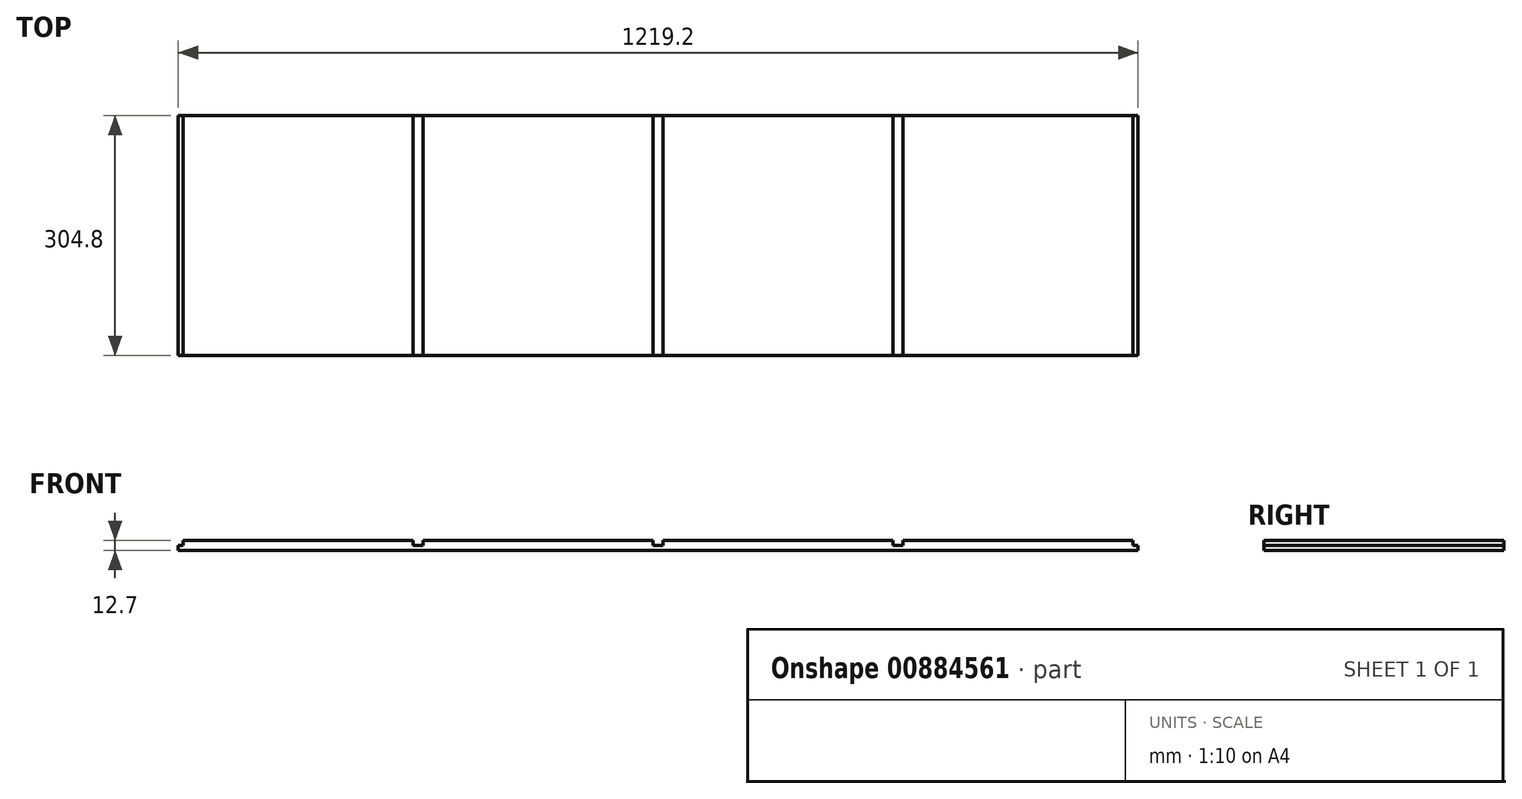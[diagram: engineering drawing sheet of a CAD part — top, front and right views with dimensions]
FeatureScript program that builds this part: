
annotation { "Feature Type Name" : "Feature", "Feature Type Description" : "" }
export const myFeature = defineFeature(function(context is Context, id is Id, definition is map)
    precondition{}
    {
        {
            var Q0;
            Q0=qCreatedBy(makeId("Top.planeOp"),FACE);
            var sketch = newSketch(context, id + "F0", { "sketchPlane" : qUnion([Q0])});
            skLineSegment(sketch, "E0.bottom", {"start": v(-609.6, -152.4) * mm, "end": v(609.6, -152.4) * mm});
            skLineSegment(sketch, "E0.top", {"start": v(-609.6, 152.4) * mm, "end": v(609.6, 152.4) * mm});
            skLineSegment(sketch, "E0.left", {"start": v(-609.6, -152.4) * mm, "end": v(-609.6, 152.4) * mm});
            skLineSegment(sketch, "E0.right", {"start": v(609.6, -152.4) * mm, "end": v(609.6, 152.4) * mm});
            skPoint(sketch, "E0.middle", {"position": v(0, 0) * mm});
            skSolve(sketch);
        }
        {
            var Q0;
            Q0 = qSketchRegion(id + "F0", true);
            extrude(context, id + "F1", {"entities" : qUnion([Q0]), "endBound" : BoundingType.SYMMETRIC, "depth" : 12.7 * mm, "offsetDistance" : 25.4 * mm});
        }
        {
            var Q0;
            Q0=qCreatedBy(makeId("Front.planeOp"),FACE);
            var sketch = newSketch(context, id + "F2", { "sketchPlane" : qUnion([Q0])});
            skLineSegment(sketch, "E1.bottom", {"start": v(-298.45, 0) * mm, "end": v(-311.15, 0) * mm});
            skLineSegment(sketch, "E1.top", {"start": v(-298.45, 6.35) * mm, "end": v(-311.15, 6.35) * mm});
            skLineSegment(sketch, "E1.left", {"start": v(-298.45, 0) * mm, "end": v(-298.45, 6.35) * mm});
            skLineSegment(sketch, "E1.right", {"start": v(-311.15, 0) * mm, "end": v(-311.15, 6.35) * mm});
            skLineSegment(sketch, "E2.1.0.0", {"start": v(6.35, 6.35) * mm, "end": v(-6.35, 6.35) * mm});
            skLineSegment(sketch, "E2.1.0.1", {"start": v(6.35, 0) * mm, "end": v(-6.35, 0) * mm});
            skLineSegment(sketch, "E2.1.0.2", {"start": v(-6.35, 0) * mm, "end": v(-6.35, 6.35) * mm});
            skLineSegment(sketch, "E2.1.0.3", {"start": v(6.35, 0) * mm, "end": v(6.35, 6.35) * mm});
            skLineSegment(sketch, "E2.2.0.0", {"start": v(311.15, 6.35) * mm, "end": v(298.45, 6.35) * mm});
            skLineSegment(sketch, "E2.2.0.1", {"start": v(311.15, 0) * mm, "end": v(298.45, 0) * mm});
            skLineSegment(sketch, "E2.2.0.2", {"start": v(298.45, 0) * mm, "end": v(298.45, 6.35) * mm});
            skLineSegment(sketch, "E2.2.0.3", {"start": v(311.15, 0) * mm, "end": v(311.15, 6.35) * mm});
            skLineSegment(sketch, "E2.direction1", {"start": v(-311.15, 0) * mm, "end": v(-6.35, 0) * mm, "construction": true});
            skLineSegment(sketch, "E3.bottom", {"start": v(-603.25, 0) * mm, "end": v(-609.6, 0) * mm});
            skLineSegment(sketch, "E3.top", {"start": v(-603.25, 6.35) * mm, "end": v(-609.6, 6.35) * mm});
            skLineSegment(sketch, "E3.left", {"start": v(-603.25, 0) * mm, "end": v(-603.25, 6.35) * mm});
            skLineSegment(sketch, "E3.right", {"start": v(-609.6, 0) * mm, "end": v(-609.6, 6.35) * mm});
            skLineSegment(sketch, "E4.MirrorCS", {"start": v(603.25, 6.35) * mm, "end": v(609.6, 6.35) * mm});
            skLineSegment(sketch, "E5.MirrorCS", {"start": v(603.25, 0) * mm, "end": v(603.25, 6.35) * mm});
            skLineSegment(sketch, "E6.MirrorCS", {"start": v(603.25, 0) * mm, "end": v(609.6, 0) * mm});
            skLineSegment(sketch, "E7.MirrorCS", {"start": v(609.6, 0) * mm, "end": v(609.6, 6.35) * mm});
            skSolve(sketch);
        }
        {
            var Q0;
            Q0 = qSketchRegion(id + "F2", true);
            extrude(context, id + "F3", {"entities" : qUnion([Q0]), "operationType" : NewBodyOperationType.REMOVE, "endBound" : BoundingType.SYMMETRIC, "depth" : 304.8 * mm, "offsetDistance" : 25.4 * mm});
        }
    });
